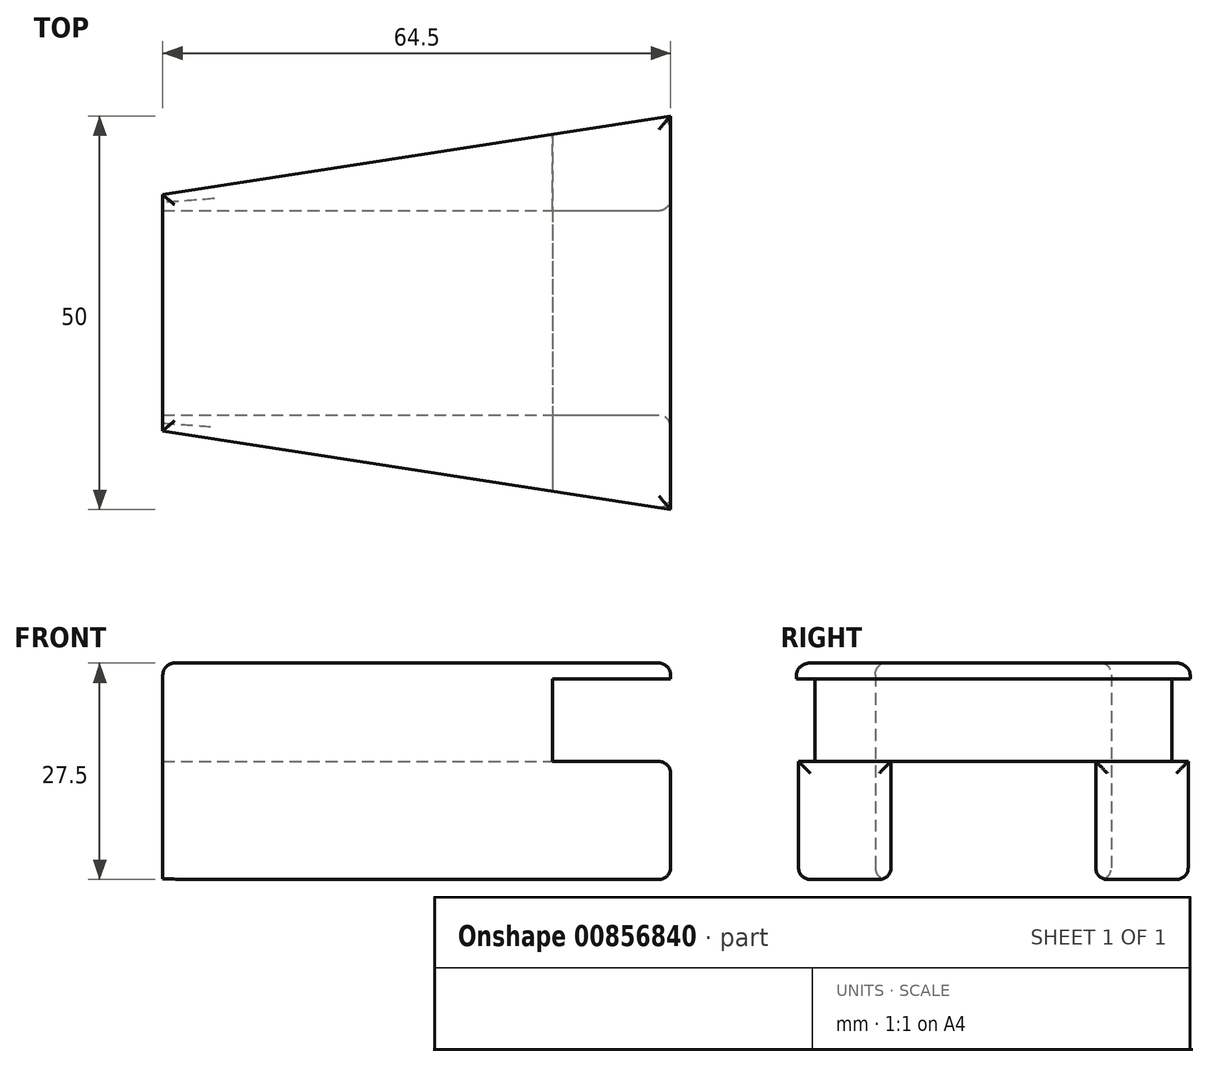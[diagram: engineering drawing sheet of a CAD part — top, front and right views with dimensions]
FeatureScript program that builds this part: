
annotation { "Feature Type Name" : "Feature", "Feature Type Description" : "" }
export const myFeature = defineFeature(function(context is Context, id is Id, definition is map)
    precondition{}
    {
        {
            var Q0;
            Q0=qCreatedBy(makeId("Top.planeOp"),FACE);
            var sketch = newSketch(context, id + "F0", { "sketchPlane" : qUnion([Q0])});
            skLineSegment(sketch, "E0", {"start": v(-64.5, 0) * mm, "end": v(-64.5, -15) * mm});
            skLineSegment(sketch, "E1", {"start": v(0, -25) * mm, "end": v(-64.5, -15) * mm});
            skLineSegment(sketch, "E2", {"start": v(0, -25) * mm, "end": v(0, 0) * mm});
            skLineSegment(sketch, "E3", {"start": v(0, 0) * mm, "end": v(-64.5, 0) * mm});
            skLineSegment(sketch, "E4.bottom", {"start": v(-64.5, -15) * mm, "end": v(0, -15) * mm});
            skLineSegment(sketch, "E4.top", {"start": v(-64.5, -13) * mm, "end": v(0, -13) * mm});
            skLineSegment(sketch, "E4.left", {"start": v(-64.5, -15) * mm, "end": v(-64.5, -13) * mm});
            skLineSegment(sketch, "E4.right", {"start": v(0, -15) * mm, "end": v(0, -13) * mm});
            skSolve(sketch);
        }
        {
            var Q0;
            {var subQ0=sQuery(id+"F0.wireOp",EDGE,"E3");Q0=makeQuery(id+"F0.imprint","IMPRINT",FACE,{"disambiguationData":[TD([[makeQuery(id+"F0.imprint","IMPRINT",EDGE,{"derivedFrom":subQ0}),1.0]])]});}
            var Q1;
            {var subQ0=sQuery(id+"F0.wireOp",EDGE,"E4.bottom");Q1=makeQuery(id+"F0.imprint","IMPRINT",FACE,{"disambiguationData":[TD([[makeQuery(id+"F0.imprint","IMPRINT",EDGE,{"derivedFrom":subQ0}),1.0]])]});}
            var Q2;
            {var subQ0=sQuery(id+"F0.wireOp",EDGE,"E1");Q2=makeQuery(id+"F0.imprint","IMPRINT",FACE,{"disambiguationData":[TD([[makeQuery(id+"F0.imprint","IMPRINT",EDGE,{"derivedFrom":subQ0}),-1.0]])]});}
            var Q3;
            {var subQ5=sQuery(id+"F0.wireOp",EDGE,"TPjvGuRz-IBh7-5pxQ-0AA6-V7IkFl4NWbCU.bottom");Q3=makeQuery(id+"F0.imprint","IMPRINT",FACE,{"disambiguationData":[TD([[makeQuery(id+"F0.imprint","IMPRINT",EDGE,{"derivedFrom":subQ5}),1.0]])]});}
            var Q4;
            {var subQ0=sQuery(id+"F0.wireOp",EDGE,"0gHiLoAS-jyIO-zUV0-tdhb-IIKy90PRcnQl");Q4=makeQuery(id+"F0.imprint","IMPRINT",FACE,{"disambiguationData":[TD([[makeQuery(id+"F0.imprint","IMPRINT",EDGE,{"derivedFrom":subQ0}),-1.0]])]});}
            extrude(context, id + "F1", {"entities" : qUnion([Q0, Q1, Q2, Q3, Q4]), "depth" : 12.5 * mm, "offsetDistance" : 25 * mm});
        }
        {
            var Q0;
            {var subQ0=sQuery(id+"F0.wireOp",EDGE,"E4.bottom");Q0=makeQuery(id+"F0.imprint","IMPRINT",FACE,{"disambiguationData":[TD([[makeQuery(id+"F0.imprint","IMPRINT",EDGE,{"derivedFrom":subQ0}),1.0]])]});}
            var Q1;
            {var subQ0=sQuery(id+"F0.wireOp",EDGE,"E1");Q1=makeQuery(id+"F0.imprint","IMPRINT",FACE,{"disambiguationData":[TD([[makeQuery(id+"F0.imprint","IMPRINT",EDGE,{"derivedFrom":subQ0}),-1.0]])]});}
            var Q2;
            {var subQ5=sQuery(id+"F0.wireOp",EDGE,"TPjvGuRz-IBh7-5pxQ-0AA6-V7IkFl4NWbCU.bottom");Q2=makeQuery(id+"F0.imprint","IMPRINT",FACE,{"disambiguationData":[TD([[makeQuery(id+"F0.imprint","IMPRINT",EDGE,{"derivedFrom":subQ5}),1.0]])]});}
            extrude(context, id + "F2", {"entities" : qUnion([Q0, Q1, Q2]), "operationType" : NewBodyOperationType.ADD, "oppositeDirection" : true, "depth" : 15 * mm, "offsetDistance" : 25 * mm});
        }
        {
            var Q0;
            {var subQ0=sQuery(id+"F0.wireOp",EDGE,"E2");Q0=makeQuery(id+"F2.boolean.opBoolean","MERGE",FACE,{"derivedFrom":[makeQuery(id+"F1.opExtrude","SWEPT_FACE",FACE,{"disambiguationData":[OSD([subQ0])]}),makeQuery(id+"F2.opExtrude","SWEPT_FACE",FACE,{"disambiguationData":[OSD([subQ0])]})]});}
            var sketch = newSketch(context, id + "F3", { "sketchPlane" : qUnion([Q0])});
            skLineSegment(sketch, "E5.bottom", {"start": v(0, 0) * mm, "end": v(-25, 0) * mm});
            skLineSegment(sketch, "E5.top", {"start": v(0, 10.5) * mm, "end": v(-25, 10.5) * mm});
            skLineSegment(sketch, "E5.left", {"start": v(0, 0) * mm, "end": v(0, 10.5) * mm});
            skLineSegment(sketch, "E5.right", {"start": v(-25, 0) * mm, "end": v(-25, 10.5) * mm});
            skSolve(sketch);
        }
        {
            var Q0;
            Q0=makeQuery(id+"F3.imprint","IMPRINT",FACE,{"disambiguationData":[TD([[makeQuery(id+"F3.imprint","IMPRINT",EDGE,{"derivedFrom":sQuery(id+"F3.wireOp",EDGE,"E5.top")}),1.0]])]});
            extrude(context, id + "F4", {"entities" : qUnion([Q0]), "operationType" : NewBodyOperationType.REMOVE, "oppositeDirection" : true, "depth" : 15 * mm, "offsetDistance" : 25 * mm});
        }
        {
            var Q0;
            Q0=makeQuery(id+"F1.opExtrude","SWEPT_BODY",BODY,{"disambiguationData":[OSD([sQuery(id+"F0.wireOp",EDGE,"E0"),sQuery(id+"F0.wireOp",EDGE,"E1"),sQuery(id+"F0.wireOp",EDGE,"E2"),sQuery(id+"F0.wireOp",EDGE,"E3")])]});
            var Q1;
            Q1=qCreatedBy(makeId("Front.planeOp"),FACE);
            mirror(context, id + "F5", {"operationType" : NewBodyOperationType.ADD, "entities" : qUnion([Q0]), "mirrorPlane" : qUnion([Q1])});
        }
        {
            var Q0;
            {var subQ0=makeQuery(id+"F1.opExtrude","CAP_FACE",FACE,{"disambiguationData":[OSD([sQuery(id+"F0.wireOp",EDGE,"E0"),sQuery(id+"F0.wireOp",EDGE,"E1"),sQuery(id+"F0.wireOp",EDGE,"E2"),sQuery(id+"F0.wireOp",EDGE,"E3")])],"isStart":false});Q0=makeQuery(id+"F5.boolean.opBoolean","MERGE",FACE,{"derivedFrom":[subQ0,makeQuery(id+"F5.opPattern","COPY",FACE,{"derivedFrom":subQ0,"instanceName":"1"})]});}
            var Q1;
            Q1=makeQuery(id+"F2.opExtrude","CAP_FACE",FACE,{"disambiguationData":[OSD([sQuery(id+"F0.wireOp",EDGE,"E0"),sQuery(id+"F0.wireOp",EDGE,"E1"),sQuery(id+"F0.wireOp",EDGE,"E2"),sQuery(id+"F0.wireOp",EDGE,"E4.top")])],"isStart":false});
            var Q2;
            Q2=makeQuery(id+"F5.opPattern","COPY",FACE,{"derivedFrom":makeQuery(id+"F2.opExtrude","CAP_FACE",FACE,{"disambiguationData":[OSD([sQuery(id+"F0.wireOp",EDGE,"E0"),sQuery(id+"F0.wireOp",EDGE,"E1"),sQuery(id+"F0.wireOp",EDGE,"E2"),sQuery(id+"F0.wireOp",EDGE,"E4.top")])],"isStart":false}),"instanceName":"1"});
            var Q3;
            {var subQ0=sQuery(id+"F0.wireOp",EDGE,"E4.top");var subQ2=sQuery(id+"F0.wireOp",EDGE,"E2");Q3=makeQuery(id+"F4.boolean.opBoolean","SPLIT",FACE,{"disambiguationData":[TD([makeQuery(id+"F2.opExtrude","SWEPT_FACE",FACE,{"disambiguationData":[OSD([subQ0])]})])],"derivedFrom":makeQuery(id+"F2.boolean.opBoolean","MERGE",FACE,{"derivedFrom":[makeQuery(id+"F1.opExtrude","SWEPT_FACE",FACE,{"disambiguationData":[OSD([subQ2])]}),makeQuery(id+"F2.opExtrude","SWEPT_FACE",FACE,{"disambiguationData":[OSD([subQ2])]})]})});}
            var Q4;
            {var subQ0=sQuery(id+"F0.wireOp",EDGE,"E4.top");var subQ2=sQuery(id+"F0.wireOp",EDGE,"E2");Q4=makeQuery(id+"F5.opPattern","COPY",FACE,{"derivedFrom":makeQuery(id+"F4.boolean.opBoolean","SPLIT",FACE,{"disambiguationData":[TD([makeQuery(id+"F2.opExtrude","SWEPT_FACE",FACE,{"disambiguationData":[OSD([subQ0])]})])],"derivedFrom":makeQuery(id+"F2.boolean.opBoolean","MERGE",FACE,{"derivedFrom":[makeQuery(id+"F1.opExtrude","SWEPT_FACE",FACE,{"disambiguationData":[OSD([subQ2])]}),makeQuery(id+"F2.opExtrude","SWEPT_FACE",FACE,{"disambiguationData":[OSD([subQ2])]})]})}),"instanceName":"1"});}
            fillet(context, id + "F6", {"entities" : qUnion([Q0, Q1, Q2, Q3, Q4]), "radius" : 1.5 * mm, "tangentPropagation" : true, "allowEdgeOverflow" : false});
        }
    });
